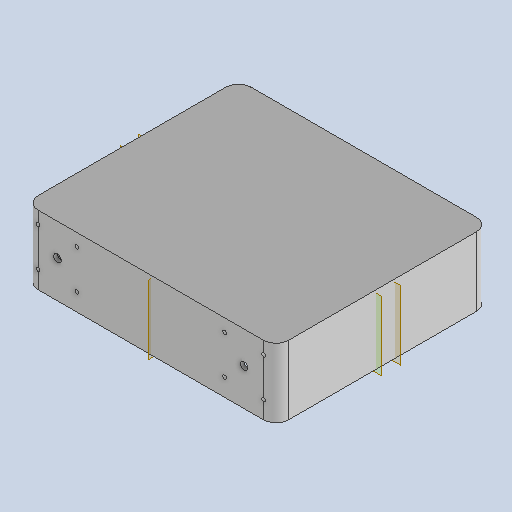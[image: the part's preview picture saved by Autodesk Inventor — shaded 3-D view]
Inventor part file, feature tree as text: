
AUTODESK INVENTOR PART (.ipt)
format: ipt  version: 2024 (Build 280153000, 153)  size: 721,408 bytes
history: native  units: mm
features: extrude x7, sketch x7, other x5, plane x4, reference x4, mirror x3, chamfer x2, projected_geometry x2, fillet x1
ambient origin geometry x8: Origin, YZ Plane, XZ Plane, XY Plane, X Axis, Y Axis, Z Axis, Center Point
bodies: Solid1 (feature_tree)
feature tree (35):
  plane  "Work Plane1"
  extrude  "Extrusion1"  Depth=2.5mm
  extrude  "Extrusion2"  Depth=2.5mm
  extrude  "Extrusion3"  Depth=20.5mm
  chamfer  "Chamfer1"  Distance=40.0mm
  chamfer  "Chamfer2"  Distance=5.0mm
  fillet  "Fillet5"  Radius=5.0mm
  extrude  "Extrusion9"  Depth=0.5mm TaperAngle=0.0deg
  plane  "Work Plane2"
  plane  "Work Plane3"
  mirror  "Mirror2"
  extrude  "Extrusion10"  Depth=5.0mm TaperAngle=45.0deg
  mirror  "Mirror4"
  plane  "Work Plane4"
  mirror  "Mirror5"
  extrude  "Extrusion11"  Depth=5.0mm TaperAngle=45.0deg
  extrude  "Extrusion12"  Depth=10.0mm
  sketch  "Sketch1"  dims[d0=2.5mm d1=2.5mm]
  reference  "Reference1"
  reference  "Reference2"
  reference  "Reference3"
  reference  "Reference4"
  sketch  "Sketch2"  dims[d2=2.5mm d3=2.5mm]
  sketch  "Sketch3"  dims[d4=41.0mm d5=20.5mm]
  projected_geometry  "Projected Loop1"
  sketch  "Sketch11"  dims[d6=10.0mm]
  projected_geometry  "Projected Loop2"
  sketch  "Sketch12"  dims[d7=20.0mm d8=40.0mm d9=0.0mm]
  sketch  "Sketch14"  dims[d10=200.0mm]
  sketch  "Sketch15"  dims[d11=170.0mm d12=5.0mm d13=0.0mm d14=5.0mm d15=50.0mm d16=0.0mm d29=5.0mm d30=2.0mm d31=45.0deg d32=5.0mm d33=2.0mm d34=45.0deg d69=10.0mm d78=31.0mm d79=31.0mm d80=3.0mm d81=3.0mm d82=3.0mm d83=3.0mm d84=10.0mm d85=5.0mm d86=10.0mm d87=0.0mm d88=6.0mm d89=70.0mm d90=95.0mm d91=22.0mm d92=2.0mm d93=0.0mm d94=75.0mm d97=5.0mm d98=2.5mm d99=5.0mm d100=2.5mm d101=5.0mm d102=2.5mm d103=5.0mm d104=2.5mm d105=75.0mm d106=83.0mm d107=48.0mm d108=14.0mm d109=14.0mm d110=50.0mm d111=10.0mm d112=0.0mm d113=5.0mm d114=0.0mm d115=15.0mm d116=15.0mm d117=58.5mm d118=17.0mm d119=5.0mm d120=0.0mm d121=15.0mm d122=12.0mm d123=0.0mm d124=29.5mm d64=0.5mm d65=0.872665mm d66=0.5mm d67=0.872665mm]
  other  "<userpath> windows\Documents\Inventor\Robotska_roka\Assembly4.iam"
  other  "Assembly4.iam"
  other  "Servo Motor MG996R  With Attachments:1"
  other  "servoMotorMG996R_7"
  other  "servoMotorMG996R_1"
